# Revit family: CORS
name_source: partatom
category: Lighting Fixtures
units: mm (PartAtom-declared; Revit-internal decimal feet)

## family parameters
Cut with Voids When Loaded = No
Host = Face
Light Source = Yes
OmniClass Number = 23.80.70.11.11
OmniClass Title = General Luminaries, Non Directional
Part Type = Normal
Room Calculation Point = No
Round Connector Dimension = Use Diameter
Shared = No

## types (1)
- CORS
    Apparent Load = 1 VA
    Body = Paint - Matte White
    Certification = UL924
    Color Filter = 16777215
    Default Elevation = 48 "
    Description = The COR Series LED Outdoor Remote offers energy efficient LEDs in an attractive single or double-head remote. Lamp-heads are fully adjustable and gasketed for outdoor operation.
    Dimming Lamp Color Temperature Shift = <None>
    Features = Single or double remote heads with base plate
Fully gasketed, waterproof construction
LED life-cycle of more than 10 years
Quick installation
Fully adjustable lamp-heads
    Glass = Glass -  White
    Height = 6.7 "
    Lamp = LED
    Manufacturer = Compass Products
    Model = CORS
    Photometric Note = For more photometric file please find the above link
    Photometric Web File = compass_led.ies
    Steel = Metal-Galvanized_Steel
    Tilt Angle = 0.00°
    Type Comments = Light Fixture
    URL = www.currentlighting.com/compass
    Warranty = 2 year full unit warranty
    Wattage Comments = 1W
    Width = 4.5 "

## geometry (parser evidence)
native form markers: Sweep x2
no freeform markers — native parametric forms only
